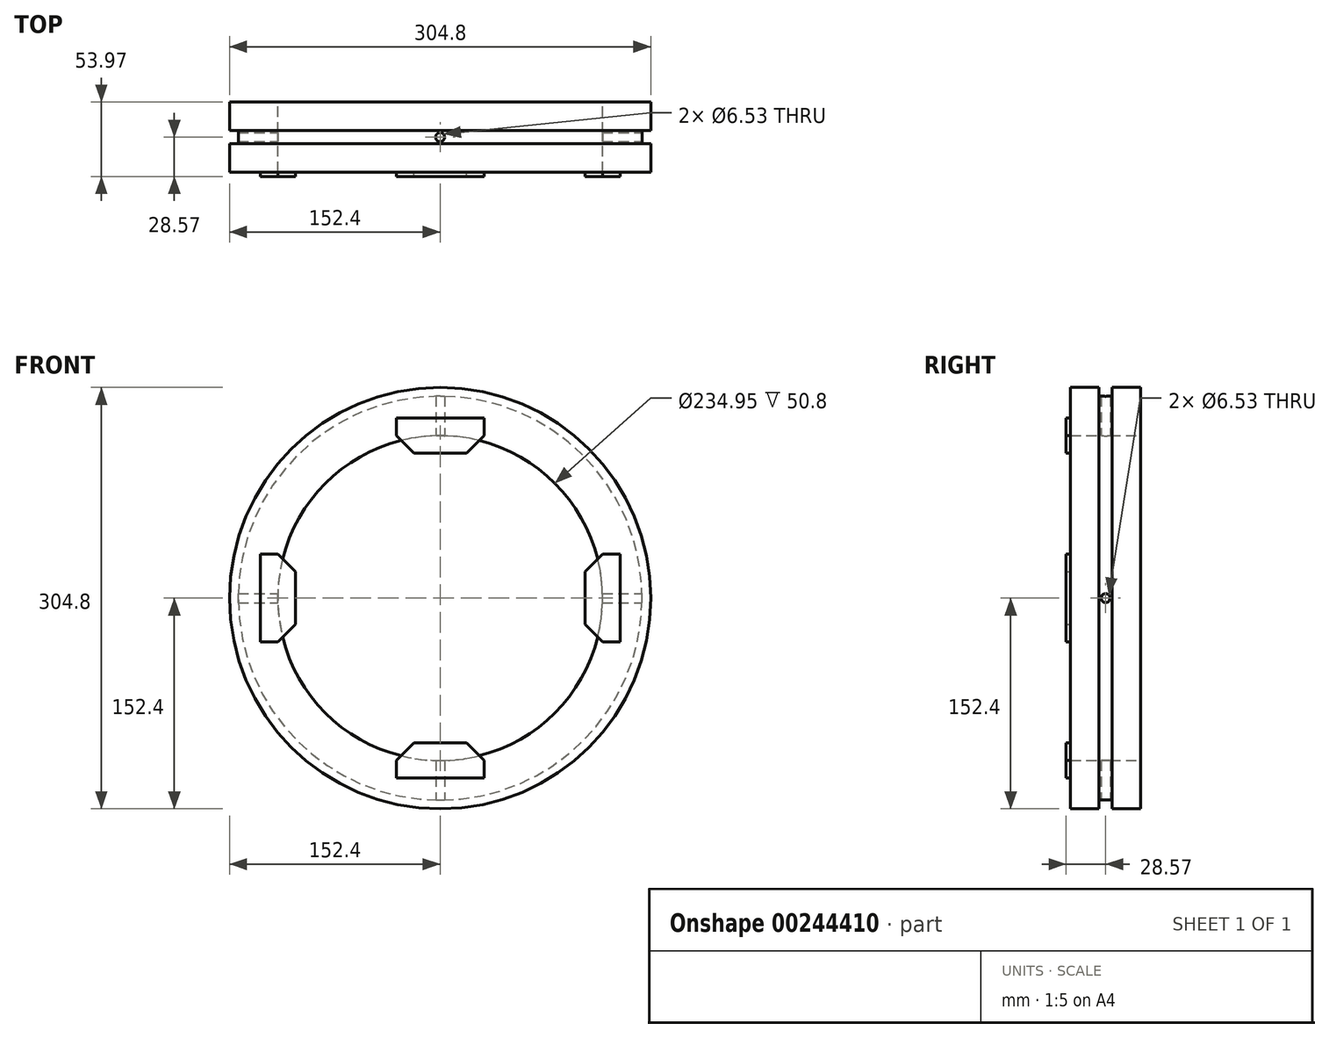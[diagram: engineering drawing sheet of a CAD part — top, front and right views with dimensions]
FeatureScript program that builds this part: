
annotation { "Feature Type Name" : "Feature", "Feature Type Description" : "" }
export const myFeature = defineFeature(function(context is Context, id is Id, definition is map)
    precondition{}
    {
        {
            var Q0;
            Q0=qCreatedBy(makeId("Front.planeOp"),FACE);
            var sketch = newSketch(context, id + "F0", { "sketchPlane" : qUnion([Q0])});
            skCircle(sketch, "E0", {"center": v(0, 0) * mm, "radius": 152.4 * mm});
            skCircle(sketch, "E1", {"center": v(0, 0) * mm, "radius": 117.48 * mm});
            skSolve(sketch);
        }
        {
            var Q0;
            Q0 = qSketchRegion(id + "F0", true);
            extrude(context, id + "F1", {"entities" : qUnion([Q0]), "endBound" : BoundingType.SYMMETRIC, "depth" : 50.8 * mm});
        }
        {
            var Q0;
            Q0=qCreatedBy(makeId("Top.planeOp"),FACE);
            var sketch = newSketch(context, id + "F2", { "sketchPlane" : qUnion([Q0])});
            skLineSegment(sketch, "E2.bottom", {"start": v(-152.4, -4.76) * mm, "end": v(-146.05, -4.76) * mm});
            skLineSegment(sketch, "E2.top", {"start": v(-152.4, 4.76) * mm, "end": v(-146.05, 4.76) * mm});
            skLineSegment(sketch, "E2.left", {"start": v(-152.4, -4.76) * mm, "end": v(-152.4, 4.76) * mm});
            skLineSegment(sketch, "E2.right", {"start": v(-146.05, -4.76) * mm, "end": v(-146.05, 4.76) * mm});
            skLineSegment(sketch, "E3", {"start": v(-152.4, -47.37) * mm, "end": v(-152.4, 56.11) * mm, "construction": true});
            skLineSegment(sketch, "E4", {"start": v(0, -64.65) * mm, "end": v(0, 52.87) * mm, "construction": true});
            skSolve(sketch);
        }
        {
            var Q0;
            Q0 = qSketchRegion(id + "F2", true);
            var Q1;
            Q1=sQuery(id+"F2.wireOp",EDGE,"E4");
            revolve(context, id + "F3", {"operationType" : NewBodyOperationType.REMOVE, "entities" : qUnion([Q0]), "axis" : qUnion([Q1]), "revolveType" : RevolveType.FULL, "oppositeDirection" : true});
        }
        {
            var Q0;
            Q0=qCreatedBy(makeId("Top.planeOp"),FACE);
            cPlane(context, id + "F4", {"entities" : qUnion([Q0]), "cplaneType" : CPlaneType.OFFSET, "offset" : 152.4 * mm, "oppositeDirection" : true, "width" : 152.4 * mm, "height" : 152.4 * mm});
        }
        {
            var Q0;
            Q0=qCreatedBy(id+"F4.planeOp",FACE);
            var sketch = newSketch(context, id + "F5", { "sketchPlane" : qUnion([Q0])});
            skPoint(sketch, "E5", {"position": v(0, 0) * mm});
            skSolve(sketch);
        }
        {
            var Q0;
            Q0=sQuery(id+"F5.wireOp",VERTEX,"E5");
            var Q1;
            Q1=makeQuery(id+"F1.opExtrude","SWEPT_BODY",BODY,{"disambiguationData":[OSD([sQuery(id+"F0.wireOp",EDGE,"E0"),sQuery(id+"F0.wireOp",EDGE,"E1")])]});
            hole(context, id + "F6", {"style" : HoleStyle.SIMPLE, "endStyle" : HoleEndStyle.THROUGH, "oppositeDirection" : true, "standardTappedOrClearance" : lookupTablePath({ "standard" : "ANSI", "engagement" : "75%", "pitch" : "18 tpi", "size" : "5/16", "type" : "Tapped" }), "standardBlindInLast" : lookupTablePath({ "standard" : "ANSI", "engagement" : "75%", "pitch" : "18 tpi", "size" : "5/16", "type" : "Tapped" }), "holeDiameter" : 6.53 * mm, "showTappedDepth" : true, "tappedDepth" : 12.7 * mm, "tapClearance" : 3, "startFromSketch" : true, "locations" : qUnion([Q0]), "scope" : qUnion([Q1]), "majorDiameter" : 7.94 * mm});
        }
        {
            var Q0;
            Q0=qCreatedBy(makeId("Right.planeOp"),FACE);
            cPlane(context, id + "F7", {"entities" : qUnion([Q0]), "cplaneType" : CPlaneType.OFFSET, "offset" : 152.4 * mm, "width" : 152.4 * mm, "height" : 152.4 * mm});
        }
        {
            var Q0;
            Q0=qCreatedBy(id+"F7.planeOp",FACE);
            var sketch = newSketch(context, id + "F8", { "sketchPlane" : qUnion([Q0])});
            skPoint(sketch, "E6", {"position": v(0, 0) * mm});
            skSolve(sketch);
        }
        {
            var Q0;
            Q0=sQuery(id+"F8.wireOp",VERTEX,"E6");
            var Q1;
            Q1=makeQuery(id+"F1.opExtrude","SWEPT_BODY",BODY,{"disambiguationData":[OSD([sQuery(id+"F0.wireOp",EDGE,"E0"),sQuery(id+"F0.wireOp",EDGE,"E1")])]});
            hole(context, id + "F9", {"style" : HoleStyle.SIMPLE, "endStyle" : HoleEndStyle.THROUGH, "standardTappedOrClearance" : lookupTablePath({ "standard" : "ANSI", "engagement" : "75%", "pitch" : "18 tpi", "size" : "5/16", "type" : "Tapped" }), "standardBlindInLast" : lookupTablePath({ "standard" : "ANSI", "engagement" : "75%", "pitch" : "18 tpi", "size" : "5/16", "type" : "Tapped" }), "holeDiameter" : 6.53 * mm, "showTappedDepth" : true, "tappedDepth" : 12.7 * mm, "tapClearance" : 3, "startFromSketch" : true, "locations" : qUnion([Q0]), "scope" : qUnion([Q1]), "majorDiameter" : 7.94 * mm});
        }
        {
            var Q0;
            Q0=makeQuery(id+"F1.opExtrude","CAP_FACE",FACE,{"disambiguationData":[OSD([sQuery(id+"F0.wireOp",EDGE,"E0"),sQuery(id+"F0.wireOp",EDGE,"E1")])],"isStart":false});
            var sketch = newSketch(context, id + "F10", { "sketchPlane" : qUnion([Q0])});
            skLineSegment(sketch, "E7.bottom", {"start": v(-31.75, 130.18) * mm, "end": v(31.75, 130.18) * mm});
            skLineSegment(sketch, "E7.top", {"start": v(-19.05, 104.78) * mm, "end": v(19.05, 104.78) * mm});
            skLineSegment(sketch, "E7.left", {"start": v(-31.75, 130.18) * mm, "end": v(-31.75, 117.48) * mm});
            skLineSegment(sketch, "E7.right", {"start": v(31.75, 130.18) * mm, "end": v(31.75, 117.48) * mm});
            skLineSegment(sketch, "E8", {"start": v(0, 130.18) * mm, "end": v(0, 0) * mm, "construction": true});
            skLineSegment(sketch, "E9", {"start": v(-31.75, 117.48) * mm, "end": v(-19.05, 104.78) * mm});
            skLineSegment(sketch, "E10", {"start": v(19.05, 104.78) * mm, "end": v(31.75, 117.48) * mm});
            skPoint(sketch, "E11.orphan", {"position": v(-31.75, 104.77) * mm});
            skPoint(sketch, "E12.orphan", {"position": v(31.75, 104.78) * mm});
            skLineSegment(sketch, "E13.1.0", {"start": v(-130.18, -31.75) * mm, "end": v(-130.18, 31.75) * mm});
            skLineSegment(sketch, "E13.1.1", {"start": v(-130.18, 31.75) * mm, "end": v(-117.48, 31.75) * mm});
            skLineSegment(sketch, "E13.1.2", {"start": v(-104.78, 19.05) * mm, "end": v(-117.48, 31.75) * mm});
            skLineSegment(sketch, "E13.1.3", {"start": v(-104.78, -19.05) * mm, "end": v(-104.78, 19.05) * mm});
            skLineSegment(sketch, "E13.1.4", {"start": v(-117.48, -31.75) * mm, "end": v(-104.78, -19.05) * mm});
            skLineSegment(sketch, "E13.1.5", {"start": v(-130.18, -31.75) * mm, "end": v(-117.48, -31.75) * mm});
            skLineSegment(sketch, "E13.2.0", {"start": v(31.75, -130.18) * mm, "end": v(-31.75, -130.18) * mm});
            skLineSegment(sketch, "E13.2.1", {"start": v(-31.75, -130.18) * mm, "end": v(-31.75, -117.48) * mm});
            skLineSegment(sketch, "E13.2.2", {"start": v(-19.05, -104.78) * mm, "end": v(-31.75, -117.48) * mm});
            skLineSegment(sketch, "E13.2.3", {"start": v(19.05, -104.78) * mm, "end": v(-19.05, -104.78) * mm});
            skLineSegment(sketch, "E13.2.4", {"start": v(31.75, -117.48) * mm, "end": v(19.05, -104.78) * mm});
            skLineSegment(sketch, "E13.2.5", {"start": v(31.75, -130.18) * mm, "end": v(31.75, -117.48) * mm});
            skLineSegment(sketch, "E13.3.0", {"start": v(130.18, 31.75) * mm, "end": v(130.18, -31.75) * mm});
            skLineSegment(sketch, "E13.3.1", {"start": v(130.18, -31.75) * mm, "end": v(117.48, -31.75) * mm});
            skLineSegment(sketch, "E13.3.2", {"start": v(104.78, -19.05) * mm, "end": v(117.48, -31.75) * mm});
            skLineSegment(sketch, "E13.3.3", {"start": v(104.78, 19.05) * mm, "end": v(104.78, -19.05) * mm});
            skLineSegment(sketch, "E13.3.4", {"start": v(117.48, 31.75) * mm, "end": v(104.78, 19.05) * mm});
            skLineSegment(sketch, "E13.3.5", {"start": v(130.18, 31.75) * mm, "end": v(117.48, 31.75) * mm});
            skPoint(sketch, "E13.center", {"position": v(0, 0) * mm});
            skSolve(sketch);
        }
        {
            var Q0;
            Q0 = qSketchRegion(id + "F10", true);
            extrude(context, id + "F11", {"entities" : qUnion([Q0]), "operationType" : NewBodyOperationType.ADD, "depth" : 3.17 * mm});
        }
    });
